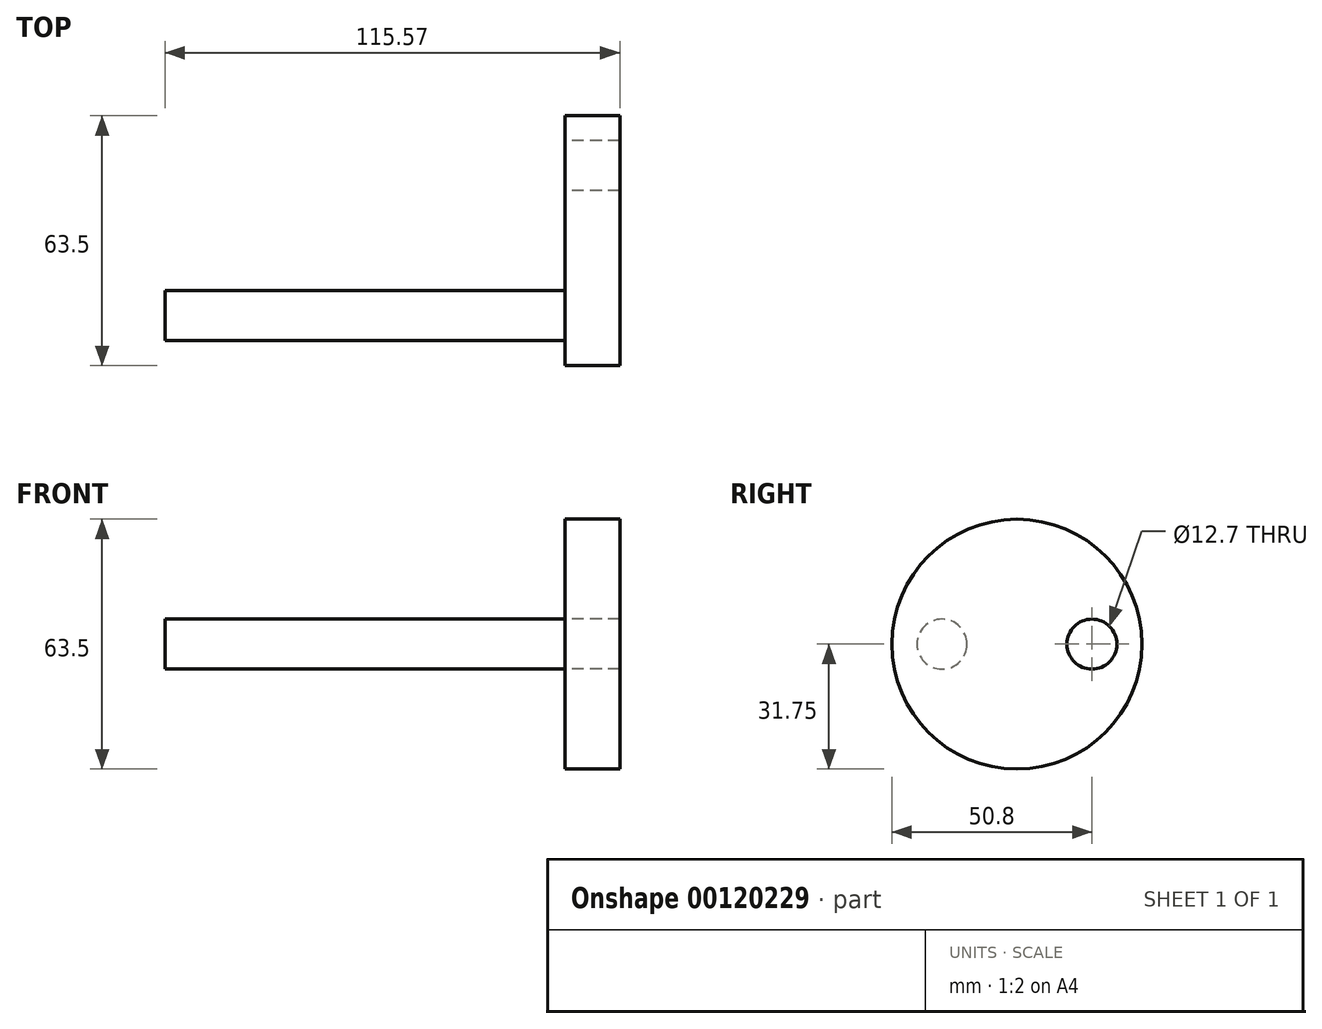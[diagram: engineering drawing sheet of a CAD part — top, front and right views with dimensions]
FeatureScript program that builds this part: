
annotation { "Feature Type Name" : "Feature", "Feature Type Description" : "" }
export const myFeature = defineFeature(function(context is Context, id is Id, definition is map)
    precondition{}
    {
        {
            var Q0;
            Q0=qCreatedBy(makeId("Front.planeOp"),FACE);
            var sketch = newSketch(context, id + "F0", { "sketchPlane" : qUnion([Q0])});
            skLineSegment(sketch, "E0.bottom", {"start": v(-50.8, 0) * mm, "end": v(50.8, 0) * mm});
            skLineSegment(sketch, "E0.top", {"start": v(-50.8, -6.35) * mm, "end": v(50.8, -6.35) * mm});
            skLineSegment(sketch, "E0.left", {"start": v(-50.8, 0) * mm, "end": v(-50.8, -6.35) * mm});
            skLineSegment(sketch, "E0.right", {"start": v(50.8, 0) * mm, "end": v(50.8, -6.35) * mm});
            skPoint(sketch, "E1.endSnap0", {"position": v(0, 0) * mm});
            skLineSegment(sketch, "E2", {"start": v(-50.8, -6.35) * mm, "end": v(50.8, -6.35) * mm, "construction": true});
            skLineSegment(sketch, "E3", {"start": v(-50.8, 0) * mm, "end": v(-163.56, 0) * mm, "construction": true});
            skSolve(sketch);
        }
        {
            var Q0;
            Q0 = qSketchRegion(id + "F0", true);
            var Q1;
            Q1=sQuery(id+"F0.wireOp",EDGE,"E3");
            revolve(context, id + "F1", {"entities" : qUnion([Q0]), "axis" : qUnion([Q1]), "revolveType" : RevolveType.FULL});
        }
        {
            var Q0;
            Q0=makeQuery(id+"F1.opRevolve","SWEPT_FACE",FACE,{"disambiguationData":[OSD([sQuery(id+"F0.wireOp",EDGE,"E0.right")])]});
            var sketch = newSketch(context, id + "F2", { "sketchPlane" : qUnion([Q0])});
            skLineSegment(sketch, "E4", {"start": v(0, 0) * mm, "end": v(50.8, 0) * mm, "construction": true});
            skLineSegment(sketch, "E5", {"start": v(0, 0) * mm, "end": v(-12.7, 0) * mm, "construction": true});
            skLineSegment(sketch, "E6", {"start": v(-12.7, 0) * mm, "end": v(50.8, 0) * mm});
            skPoint(sketch, "E7", {"position": v(19.05, 0) * mm});
            skCircle(sketch, "E8", {"center": v(19.05, 0) * mm, "radius": 31.75 * mm});
            skLineSegment(sketch, "E9", {"start": v(50.8, 0) * mm, "end": v(38.1, 0) * mm, "construction": true});
            skCircle(sketch, "E10", {"center": v(38.1, 0) * mm, "radius": 6.35 * mm});
            skSolve(sketch);
        }
        {
            var Q0;
            Q0 = qSketchRegion(id + "F2", true);
            extrude(context, id + "F3", {"entities" : qUnion([Q0]), "operationType" : NewBodyOperationType.ADD, "depth" : 13.97 * mm});
        }
        {
            var Q0;
            {var subQ0=sQuery(id+"F2.wireOp",EDGE,"E10");var subQ1=sQuery(id+"F2.wireOp",EDGE,"E6");var subQ2=makeQuery(id+"F2.imprint","INTERSECT",VERTEX,{"disambiguationData":[OD(0.0)],"derivedFrom":[subQ1,subQ0]});Q0=makeQuery(id+"F2.imprint","IMPRINT",FACE,{"disambiguationData":[TD([[makeQuery(id+"F2.imprint","IMPRINT",EDGE,{"disambiguationData":[TD([[subQ2,-1.0]])],"derivedFrom":subQ1}),-1.0]])]});}
            var Q1;
            {var subQ0=sQuery(id+"F2.wireOp",EDGE,"E10");var subQ1=sQuery(id+"F2.wireOp",EDGE,"E6");var subQ2=makeQuery(id+"F2.imprint","INTERSECT",VERTEX,{"disambiguationData":[OD(0.0)],"derivedFrom":[subQ1,subQ0]});Q1=makeQuery(id+"F2.imprint","IMPRINT",FACE,{"disambiguationData":[TD([[makeQuery(id+"F2.imprint","IMPRINT",EDGE,{"disambiguationData":[TD([[subQ2,-1.0]])],"derivedFrom":subQ1}),1.0]])]});}
            var Q2;
            Q2=sQuery(id+"F2.wireOp",EDGE,"E10");
            extrude(context, id + "F4", {"entities" : qUnion([Q0, Q1]), "surfaceEntities" : qUnion([Q2]), "depth" : 2.8 * mm});
        }
        {
            var Q0;
            Q0=makeQuery(id+"F4.opExtrude","SWEPT_BODY",BODY,{"disambiguationData":[OSD([sQuery(id+"F2.wireOp",EDGE,"E10")])]});
            deleteBodies(context, id + "F5", {"entities" : qUnion([Q0])});
        }
    });
